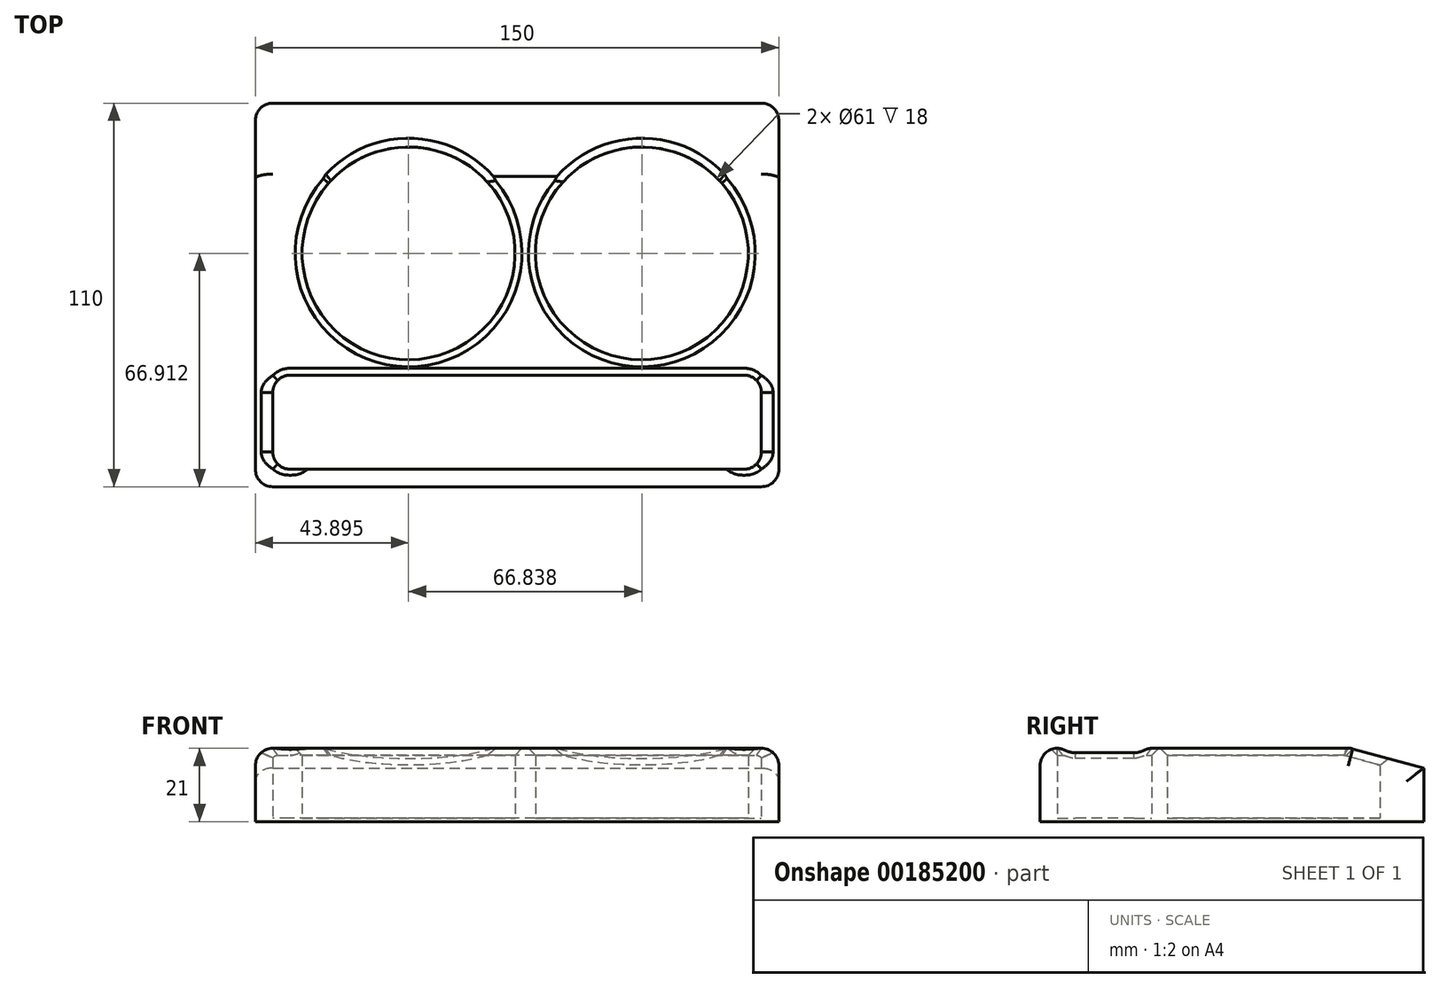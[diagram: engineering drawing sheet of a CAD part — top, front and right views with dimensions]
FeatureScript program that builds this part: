
annotation { "Feature Type Name" : "Feature", "Feature Type Description" : "" }
export const myFeature = defineFeature(function(context is Context, id is Id, definition is map)
    precondition{}
    {
        {
            var Q0;
            Q0=qCreatedBy(makeId("Top.planeOp"),FACE);
            var sketch = newSketch(context, id + "F0", { "sketchPlane" : qUnion([Q0])});
            skLineSegment(sketch, "E0.bottom", {"start": v(75, 55) * mm, "end": v(-75, 55) * mm});
            skLineSegment(sketch, "E0.top", {"start": v(75, -55) * mm, "end": v(-75, -55) * mm});
            skLineSegment(sketch, "E0.left", {"start": v(75, 55) * mm, "end": v(75, -55) * mm});
            skLineSegment(sketch, "E0.right", {"start": v(-75, 55) * mm, "end": v(-75, -55) * mm});
            skPoint(sketch, "E0.middle", {"position": v(0, 0) * mm});
            skLineSegment(sketch, "E1", {"start": v(0, 55) * mm, "end": v(0, -55) * mm, "construction": true});
            skCircle(sketch, "E2", {"center": v(-31.1, 11.91) * mm, "radius": 30.5 * mm});
            skCircle(sketch, "E3", {"center": v(35.73, 11.91) * mm, "radius": 30.5 * mm});
            skLineSegment(sketch, "E4", {"start": v(-75, 11.91) * mm, "end": v(75, 11.91) * mm, "construction": true});
            skLineSegment(sketch, "E5.bottom", {"start": v(70, -23) * mm, "end": v(-70, -23) * mm});
            skLineSegment(sketch, "E5.top", {"start": v(70, -50) * mm, "end": v(-70, -50) * mm});
            skLineSegment(sketch, "E5.left", {"start": v(70, -23) * mm, "end": v(70, -50) * mm});
            skLineSegment(sketch, "E5.right", {"start": v(-70, -23) * mm, "end": v(-70, -50) * mm});
            skPoint(sketch, "E5.middle", {"position": v(0, -36.5) * mm});
            skSolve(sketch);
        }
        {
            var Q0;
            Q0=makeQuery(id+"F0.imprint","IMPRINT",FACE,{"disambiguationData":[TD([[makeQuery(id+"F0.imprint","IMPRINT",EDGE,{"derivedFrom":sQuery(id+"F0.wireOp",EDGE,"E0.bottom")}),1.0]])]});
            var Q1;
            Q1=makeQuery(id+"F0.imprint","IMPRINT",FACE,{"disambiguationData":[TD([[makeQuery(id+"F0.imprint","IMPRINT",EDGE,{"derivedFrom":sQuery(id+"F0.wireOp",EDGE,"E2")}),1.0]])]});
            var Q2;
            Q2=makeQuery(id+"F0.imprint","IMPRINT",FACE,{"disambiguationData":[TD([[makeQuery(id+"F0.imprint","IMPRINT",EDGE,{"derivedFrom":sQuery(id+"F0.wireOp",EDGE,"E3")}),1.0]])]});
            var Q3;
            Q3=makeQuery(id+"F0.imprint","IMPRINT",FACE,{"disambiguationData":[TD([[makeQuery(id+"F0.imprint","IMPRINT",EDGE,{"derivedFrom":sQuery(id+"F0.wireOp",EDGE,"E5.bottom")}),1.0]])]});
            extrude(context, id + "F1", {"entities" : qUnion([Q0, Q1, Q2, Q3]), "oppositeDirection" : true, "depth" : 1 * mm, "offsetDistance" : 25 * mm});
        }
        {
            var Q0;
            Q0=makeQuery(id+"F0.imprint","IMPRINT",FACE,{"disambiguationData":[TD([[makeQuery(id+"F0.imprint","IMPRINT",EDGE,{"derivedFrom":sQuery(id+"F0.wireOp",EDGE,"E0.bottom")}),1.0]])]});
            extrude(context, id + "F2", {"entities" : qUnion([Q0]), "operationType" : NewBodyOperationType.ADD, "depth" : 20 * mm, "offsetDistance" : 25 * mm});
        }
        {
            var Q0;
            Q0=makeQuery(id+"F2.opExtrude","CAP_EDGE",EDGE,{"disambiguationData":[OSD([sQuery(id+"F0.wireOp",EDGE,"E0.bottom")])],"isStart":false});
            chamfer(context, id + "F3", {"entities" : qUnion([Q0]), "chamferType" : ChamferType.OFFSET_ANGLE, "width" : 21 * mm, "oppositeDirection" : true, "angle" : 15 * degree, "tangentPropagation" : true});
        }
        {
            var Q0;
            Q0=makeQuery(id+"F2.opExtrude","SWEPT_EDGE",EDGE,{"disambiguationData":[OSD([sQuery(id+"F0.wireOp",EDGE,"E5.bottom"),sQuery(id+"F0.wireOp",EDGE,"E5.right")])]});
            var Q1;
            Q1=makeQuery(id+"F2.opExtrude","SWEPT_EDGE",EDGE,{"disambiguationData":[OSD([sQuery(id+"F0.wireOp",EDGE,"E5.top"),sQuery(id+"F0.wireOp",EDGE,"E5.right")])]});
            var Q2;
            Q2=makeQuery(id+"F2.opExtrude","SWEPT_EDGE",EDGE,{"disambiguationData":[OSD([sQuery(id+"F0.wireOp",EDGE,"E5.bottom"),sQuery(id+"F0.wireOp",EDGE,"E5.left")])]});
            var Q3;
            Q3=makeQuery(id+"F2.opExtrude","SWEPT_EDGE",EDGE,{"disambiguationData":[OSD([sQuery(id+"F0.wireOp",EDGE,"E5.top"),sQuery(id+"F0.wireOp",EDGE,"E5.left")])]});
            fillet(context, id + "F4", {"entities" : qUnion([Q0, Q1, Q2, Q3]), "radius" : 5 * mm, "tangentPropagation" : true, "allowEdgeOverflow" : false});
        }
        {
            var Q0;
            {var subQ0=sQuery(id+"F0.wireOp",EDGE,"E0.right");var subQ1=sQuery(id+"F0.wireOp",EDGE,"E0.top");Q0=makeQuery(id+"F2.boolean.opBoolean","MERGE",EDGE,{"derivedFrom":[makeQuery(id+"F1.opExtrude","SWEPT_EDGE",EDGE,{"disambiguationData":[OSD([subQ1,subQ0])]}),makeQuery(id+"F2.opExtrude","SWEPT_EDGE",EDGE,{"disambiguationData":[OSD([subQ1,subQ0])]})]});}
            var Q1;
            {var subQ0=sQuery(id+"F0.wireOp",EDGE,"E0.left");var subQ1=sQuery(id+"F0.wireOp",EDGE,"E0.top");Q1=makeQuery(id+"F2.boolean.opBoolean","MERGE",EDGE,{"derivedFrom":[makeQuery(id+"F1.opExtrude","SWEPT_EDGE",EDGE,{"disambiguationData":[OSD([subQ1,subQ0])]}),makeQuery(id+"F2.opExtrude","SWEPT_EDGE",EDGE,{"disambiguationData":[OSD([subQ1,subQ0])]})]});}
            var Q2;
            {var subQ0=sQuery(id+"F0.wireOp",EDGE,"E0.left");var subQ1=sQuery(id+"F0.wireOp",EDGE,"E0.bottom");Q2=makeQuery(id+"F2.boolean.opBoolean","MERGE",EDGE,{"derivedFrom":[makeQuery(id+"F1.opExtrude","SWEPT_EDGE",EDGE,{"disambiguationData":[OSD([subQ1,subQ0])]}),makeQuery(id+"F2.opExtrude","SWEPT_EDGE",EDGE,{"disambiguationData":[OSD([subQ1,subQ0])]})]});}
            var Q3;
            {var subQ0=sQuery(id+"F0.wireOp",EDGE,"E0.right");var subQ1=sQuery(id+"F0.wireOp",EDGE,"E0.bottom");Q3=makeQuery(id+"F2.boolean.opBoolean","MERGE",EDGE,{"derivedFrom":[makeQuery(id+"F1.opExtrude","SWEPT_EDGE",EDGE,{"disambiguationData":[OSD([subQ1,subQ0])]}),makeQuery(id+"F2.opExtrude","SWEPT_EDGE",EDGE,{"disambiguationData":[OSD([subQ1,subQ0])]})]});}
            var Q4;
            {var subQ0=sQuery(id+"F0.wireOp",EDGE,"E0.right");Q4=makeQuery(id+"F3.opChamfer","BLEND_EDGE",EDGE,{"blendedFrom":[makeQuery(id+"F2.opExtrude","CAP_EDGE",EDGE,{"disambiguationData":[OSD([sQuery(id+"F0.wireOp",EDGE,"E0.bottom")])],"isStart":false}),makeQuery(id+"F2.boolean.opBoolean","MERGE",FACE,{"derivedFrom":[makeQuery(id+"F1.opExtrude","SWEPT_FACE",FACE,{"disambiguationData":[OSD([subQ0])]}),makeQuery(id+"F2.opExtrude","SWEPT_FACE",FACE,{"disambiguationData":[OSD([subQ0])]})]})],"blendedInto":[makeQuery(id+"F2.boolean.opBoolean","MERGE",FACE,{"derivedFrom":[makeQuery(id+"F1.opExtrude","SWEPT_FACE",FACE,{"disambiguationData":[OSD([subQ0])]}),makeQuery(id+"F2.opExtrude","SWEPT_FACE",FACE,{"disambiguationData":[OSD([subQ0])]})]})]});}
            var Q5;
            {var subQ0=sQuery(id+"F0.wireOp",EDGE,"E0.left");Q5=makeQuery(id+"F3.opChamfer","BLEND_EDGE",EDGE,{"blendedFrom":[makeQuery(id+"F2.opExtrude","CAP_EDGE",EDGE,{"disambiguationData":[OSD([sQuery(id+"F0.wireOp",EDGE,"E0.bottom")])],"isStart":false}),makeQuery(id+"F2.boolean.opBoolean","MERGE",FACE,{"derivedFrom":[makeQuery(id+"F1.opExtrude","SWEPT_FACE",FACE,{"disambiguationData":[OSD([subQ0])]}),makeQuery(id+"F2.opExtrude","SWEPT_FACE",FACE,{"disambiguationData":[OSD([subQ0])]})]})],"blendedInto":[makeQuery(id+"F2.boolean.opBoolean","MERGE",FACE,{"derivedFrom":[makeQuery(id+"F1.opExtrude","SWEPT_FACE",FACE,{"disambiguationData":[OSD([subQ0])]}),makeQuery(id+"F2.opExtrude","SWEPT_FACE",FACE,{"disambiguationData":[OSD([subQ0])]})]})]});}
            fillet(context, id + "F5", {"entities" : qUnion([Q0, Q1, Q2, Q3, Q4, Q5]), "radius" : 5 * mm, "tangentPropagation" : true, "allowEdgeOverflow" : false});
        }
        {
            var Q0;
            Q0=makeQuery(id+"F2.opExtrude","CAP_EDGE",EDGE,{"disambiguationData":[OSD([sQuery(id+"F0.wireOp",EDGE,"E0.top")])],"isStart":false});
            fillet(context, id + "F6", {"entities" : qUnion([Q0]), "radius" : 5 * mm, "tangentPropagation" : true, "allowEdgeOverflow" : false});
        }
        {
            var Q0;
            Q0=makeQuery(id+"F2.opExtrude","CAP_EDGE",EDGE,{"disambiguationData":[OSD([sQuery(id+"F0.wireOp",EDGE,"E2")])],"isStart":false});
            var Q1;
            Q1=makeQuery(id+"F2.opExtrude","CAP_EDGE",EDGE,{"disambiguationData":[OSD([sQuery(id+"F0.wireOp",EDGE,"E3")])],"isStart":false});
            var Q2;
            Q2=makeQuery(id+"F2.opExtrude","CAP_EDGE",EDGE,{"disambiguationData":[OSD([sQuery(id+"F0.wireOp",EDGE,"E5.bottom")])],"isStart":false});
            chamfer(context, id + "F7", {"entities" : qUnion([Q0, Q1, Q2]), "width" : 2 * mm, "tangentPropagation" : true});
        }
    });
